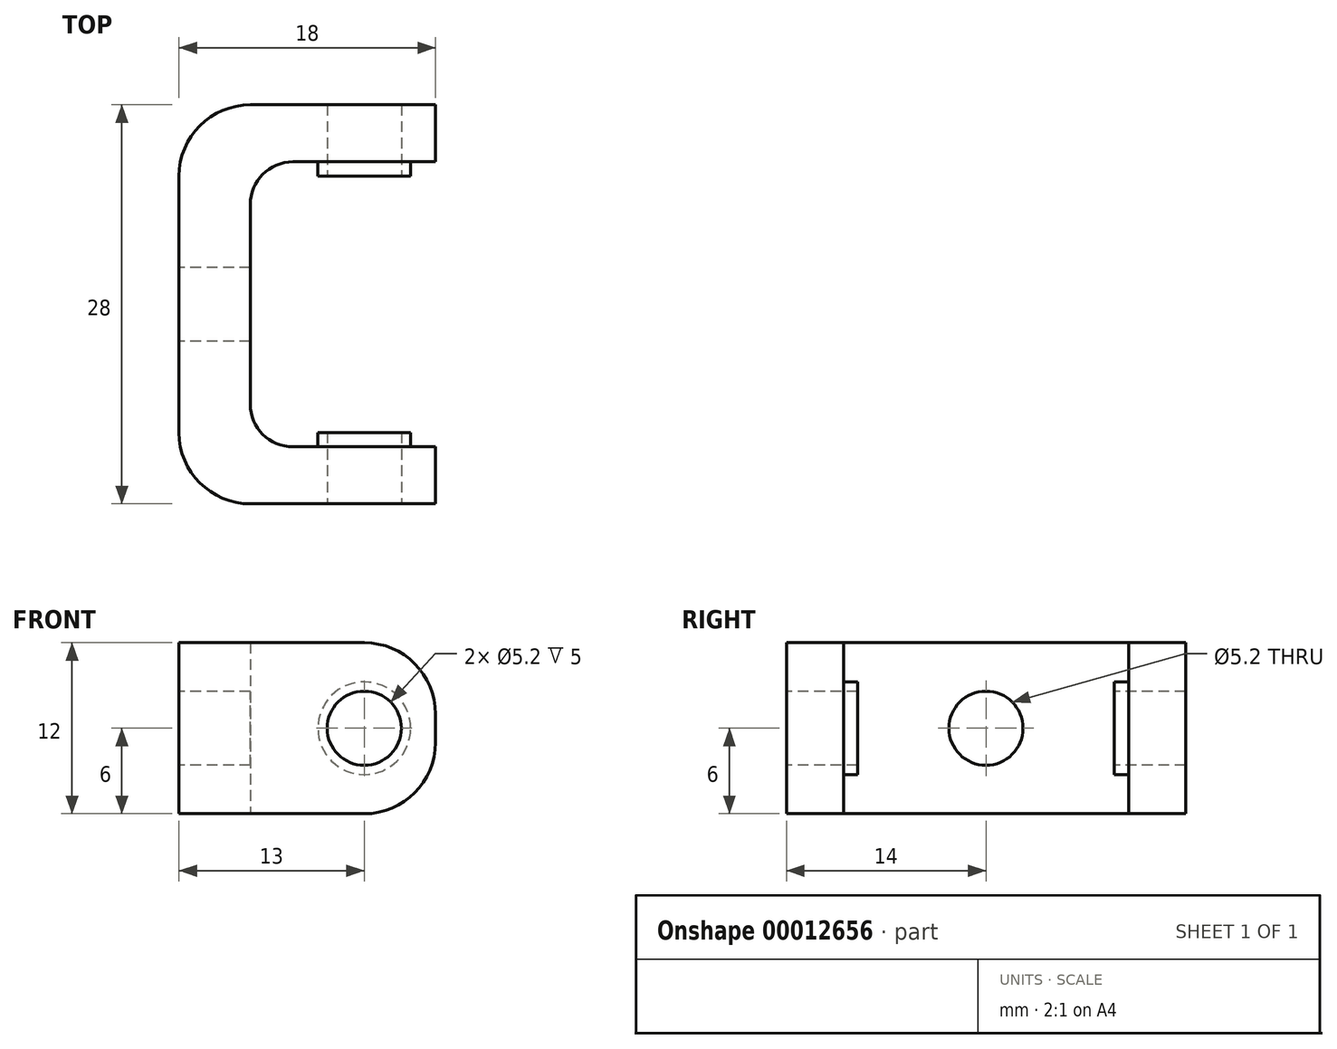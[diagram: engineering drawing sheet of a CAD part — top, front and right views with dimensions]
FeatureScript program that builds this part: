
annotation { "Feature Type Name" : "Feature", "Feature Type Description" : "" }
export const myFeature = defineFeature(function(context is Context, id is Id, definition is map)
    precondition{}
    {
        {
            var Q0;
            Q0=qCreatedBy(makeId("Top.planeOp"),FACE);
            var sketch = newSketch(context, id + "F0", { "sketchPlane" : qUnion([Q0])});
            skLineSegment(sketch, "E0.bottom", {"start": v(-8, 14) * mm, "end": v(5, 14) * mm});
            skLineSegment(sketch, "E0.left", {"start": v(-13, 9) * mm, "end": v(-13, -9) * mm});
            skLineSegment(sketch, "E1", {"start": v(5, 14) * mm, "end": v(5, 10) * mm});
            skLineSegment(sketch, "E2", {"start": v(5, 10) * mm, "end": v(-5, 10) * mm});
            skLineSegment(sketch, "E3", {"start": v(-8, 7) * mm, "end": v(-8, -7) * mm});
            skLineSegment(sketch, "E4", {"start": v(-5, -10) * mm, "end": v(5, -10) * mm});
            skLineSegment(sketch, "E5", {"start": v(5, -10) * mm, "end": v(5, -14) * mm});
            skPoint(sketch, "E6.visualSharp", {"position": v(-8, 10) * mm});
            skArc(sketch, "E6.filletArc", {"start": v(-5, 10) * mm, "mid": v(-7.12, 9.12) * mm, "end": v(-8, 7) * mm});
            skPoint(sketch, "E7.visualSharp", {"position": v(-8, -10) * mm});
            skArc(sketch, "E7.filletArc", {"start": v(-8, -7) * mm, "mid": v(-7.12, -9.12) * mm, "end": v(-5, -10) * mm});
            skLineSegment(sketch, "E8", {"start": v(-8, -14) * mm, "end": v(5, -14) * mm});
            skPoint(sketch, "E9.visualSharp", {"position": v(-13, 14) * mm});
            skArc(sketch, "E9.filletArc", {"start": v(-8, 14) * mm, "mid": v(-11.54, 12.54) * mm, "end": v(-13, 9) * mm});
            skPoint(sketch, "E10.visualSharp", {"position": v(-13, -14) * mm});
            skArc(sketch, "E10.filletArc", {"start": v(-13, -9) * mm, "mid": v(-11.54, -12.54) * mm, "end": v(-8, -14) * mm});
            skSolve(sketch);
        }
        {
            var Q0;
            Q0=qSketchRegion(id+"F0",true);
            extrude(context, id + "F1", {"entities" : qUnion([Q0]), "depth" : 6 * mm, "hasSecondDirection" : true, "secondDirectionOppositeDirection" : true, "secondDirectionDepth" : 6 * mm});
        }
        {
            var Q0;
            Q0=makeQuery(id+"F1.opExtrude","SWEPT_FACE",FACE,{"disambiguationData":[OSD([sQuery(id+"F0.wireOp",EDGE,"E0.left")])]});
            var sketch = newSketch(context, id + "F2", { "sketchPlane" : qUnion([Q0])});
            skCircle(sketch, "E11", {"center": v(0, 0) * mm, "radius": 2.6 * mm});
            skSolve(sketch);
        }
        {
            var Q0;
            Q0=qSketchRegion(id+"F2",true);
            extrude(context, id + "F3", {"entities" : qUnion([Q0]), "operationType" : NewBodyOperationType.REMOVE, "endBound" : BoundingType.UP_TO_NEXT, "oppositeDirection" : true, "depth" : 25 * mm});
        }
        {
            var Q0;
            Q0=qCreatedBy(makeId("Front.planeOp"),FACE);
            var sketch = newSketch(context, id + "F4", { "sketchPlane" : qUnion([Q0])});
            skCircle(sketch, "E12", {"center": v(0, 0) * mm, "radius": 2.6 * mm});
            skSolve(sketch);
        }
        {
            var Q0;
            Q0=qSketchRegion(id+"F4",true);
            extrude(context, id + "F5", {"entities" : qUnion([Q0]), "operationType" : NewBodyOperationType.REMOVE, "endBound" : BoundingType.THROUGH_ALL, "oppositeDirection" : true, "depth" : 25 * mm, "hasSecondDirection" : true, "secondDirectionBound" : BoundingType.THROUGH_ALL, "secondDirectionOppositeDirection" : false, "secondDirectionDepth" : 25 * mm});
        }
        {
            var Q0;
            Q0=makeQuery(id+"F1.opExtrude","CAP_EDGE",EDGE,{"disambiguationData":[OSD([sQuery(id+"F0.wireOp",EDGE,"E5")])],"isStart":false});
            var Q1;
            Q1=makeQuery(id+"F1.opExtrude","CAP_EDGE",EDGE,{"disambiguationData":[OSD([sQuery(id+"F0.wireOp",EDGE,"E5")])],"isStart":true});
            var Q2;
            Q2=makeQuery(id+"F1.opExtrude","CAP_EDGE",EDGE,{"disambiguationData":[OSD([sQuery(id+"F0.wireOp",EDGE,"E1")])],"isStart":true});
            var Q3;
            Q3=makeQuery(id+"F1.opExtrude","CAP_EDGE",EDGE,{"disambiguationData":[OSD([sQuery(id+"F0.wireOp",EDGE,"E1")])],"isStart":false});
            fillet(context, id + "F6", {"entities" : qUnion([Q0, Q1, Q2, Q3]), "radius" : 5 * mm, "tangentPropagation" : true, "allowEdgeOverflow" : false});
        }
        {
            var Q0;
            Q0=makeQuery(id+"F1.opExtrude","SWEPT_FACE",FACE,{"disambiguationData":[OSD([sQuery(id+"F0.wireOp",EDGE,"E2")])]});
            var sketch = newSketch(context, id + "F7", { "sketchPlane" : qUnion([Q0])});
            skCircle(sketch, "E13.1", {"center": v(0, 0) * mm, "radius": 2.6 * mm});
            skCircle(sketch, "E14.0", {"center": v(0, 0) * mm, "radius": 3.25 * mm});
            skSolve(sketch);
        }
        {
            var Q0;
            Q0=qSketchRegion(id+"F7",true);
            extrude(context, id + "F8", {"entities" : qUnion([Q0]), "depth" : 1 * mm});
        }
        {
            var Q0;
            Q0=makeQuery(id+"F8.opExtrude","SWEPT_BODY",BODY,{"disambiguationData":[OSD([sQuery(id+"F7.wireOp",EDGE,"E13.1"),sQuery(id+"F7.wireOp",EDGE,"E14.0")])]});
            var Q1;
            Q1=qCreatedBy(makeId("Front.planeOp"),FACE);
            mirror(context, id + "F9", {"operationType" : NewBodyOperationType.ADD, "entities" : qUnion([Q0]), "mirrorPlane" : qUnion([Q1])});
        }
    });
